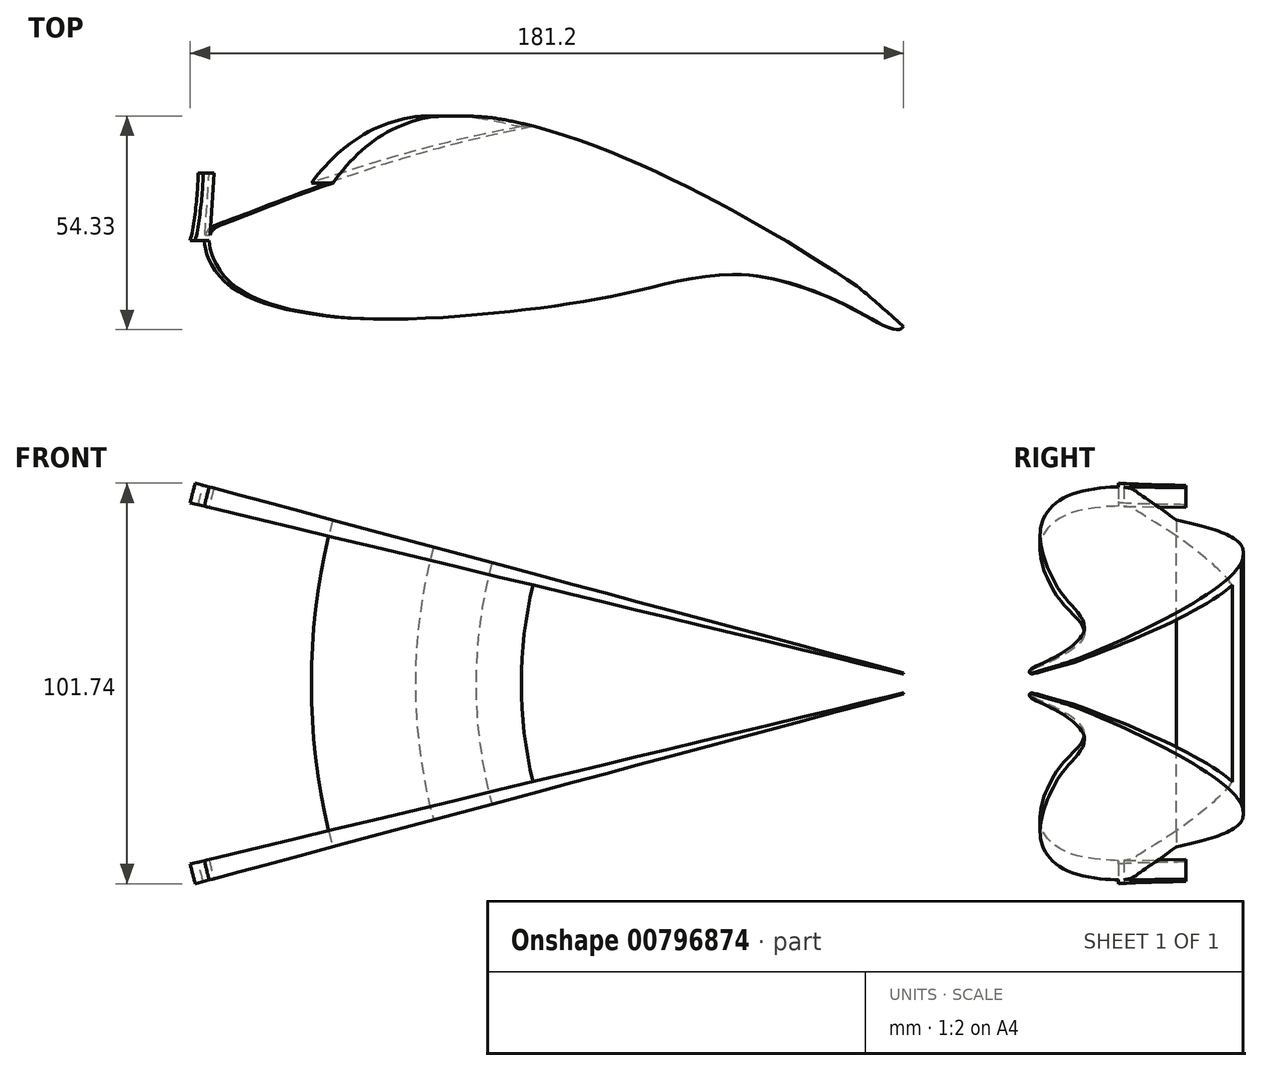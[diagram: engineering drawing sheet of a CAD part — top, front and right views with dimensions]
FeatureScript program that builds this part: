
annotation { "Feature Type Name" : "Feature", "Feature Type Description" : "" }
export const myFeature = defineFeature(function(context is Context, id is Id, definition is map)
    precondition{}
    {
        {
            var Q0;
            Q0=qCreatedBy(makeId("Top.planeOp"),FACE);
            var sketch = newSketch(context, id + "F0", { "sketchPlane" : qUnion([Q0])});
            skFitSpline(sketch, "E0", {"points": [v(-170.18, 31.8) * mm, v(-106.5, 38.35) * mm, v(-30.65, 17.74) * mm, v(27.4, -25.33) * mm, v(47.07, -59.04) * mm, v(24.6, -41.25) * mm, v(-86.84, 1.83) * mm, v(-156.13, -10.35) * mm, v(-170.18, 31.8) * mm]});
            skLineSegment(sketch, "E1", {"start": v(-156.13, -10.35) * mm, "end": v(-156.13, -10.35) * mm});
            skLineSegment(sketch, "E2", {"start": v(-156.13, 31.8) * mm, "end": v(-156.13, 31.8) * mm});
            skFitSpline(sketch, "E3", {"points": [v(-156.13, -10.35) * mm, v(-143.58, -45.36) * mm, v(-112.26, -54.53) * mm, v(-67.18, -53) * mm, v(-33.57, -46.89) * mm, v(-4.54, -43.83) * mm, v(24.49, -51.47) * mm, v(40.73, -54.96) * mm, v(24.6, -41.25) * mm, v(-86.84, 1.83) * mm, v(-128.3, -41.25) * mm], "startDerivative": vector(76.26, -423.63) * mm, "endDerivative": vector(-240.52, -486.65) * mm});
            skLineSegment(sketch, "E4", {"start": v(47.07, -59.04) * mm, "end": v(47.07, -80.17) * mm});
            skLineSegment(sketch, "E5", {"start": v(47.07, -59.04) * mm, "end": v(47.07, -18.21) * mm});
            skFitSpline(sketch, "E6", {"points": [v(-156.13, 40.59) * mm, v(-151.83, 31.31) * mm, v(-148.5, 17.34) * mm, v(-147.45, -1.95) * mm, v(-148.02, -21.15) * mm, v(-151.28, -31.75) * mm, v(-156.13, 40.59) * mm]});
            skFitSpline(sketch, "E7", {"points": [v(-145.6, -31.34) * mm, v(-140.42, -40.15) * mm, v(-112.45, -48.95) * mm, v(-66.86, -47.66) * mm, v(-34.74, -42.74) * mm, v(-5.2, -38.33) * mm, v(25.36, -47.92) * mm, v(36.8, -51.47) * mm, v(0, -2.85) * mm, v(-138.35, -24.09) * mm, v(-144.57, -26.68) * mm, v(-145.6, -28.23) * mm, v(-145.6, -31.34) * mm]});
            skLineSegment(sketch, "E8", {"start": v(-145.6, -28.23) * mm, "end": v(-144.57, -12.5) * mm});
            skLineSegment(sketch, "E9", {"start": v(-149.5, -29.67) * mm, "end": v(-145.6, -29.67) * mm});
            skSolve(sketch);
        }
        {
            var Q0;
            {var subQ5=sQuery(id+"F0.wireOp",EDGE,"E3");Q0=makeQuery(id+"F0.imprint","IMPRINT",FACE,{"disambiguationData":[TD([[makeQuery(id+"F0.imprint","IMPRINT",EDGE,{"derivedFrom":subQ5}),1.0]])]});}
            var Q1;
            {var subQ5=sQuery(id+"F0.wireOp",EDGE,"E7");Q1=makeQuery(id+"F0.imprint","IMPRINT",FACE,{"disambiguationData":[TD([[makeQuery(id+"F0.imprint","IMPRINT",EDGE,{"derivedFrom":subQ5}),1.0]])]});}
            var Q2;
            {var subQ0=sQuery(id+"F0.wireOp",EDGE,"E8");Q2=makeQuery(id+"F0.imprint","IMPRINT",FACE,{"disambiguationData":[TD([[makeQuery(id+"F0.imprint","IMPRINT",EDGE,{"derivedFrom":subQ0}),1.0]])]});}
            var Q3;
            Q3=sQuery(id+"F0.wireOp",EDGE,"E5");
            revolve(context, id + "F1", {"surfaceOperationType" : NewSurfaceOperationType.NEW, "entities" : qUnion([Q0, Q1, Q2]), "axis" : qUnion([Q3]), "revolveType" : RevolveType.SYMMETRIC, "angle" : 30 * degree});
        }
        {
            var Q0;
            {var subQ5=sQuery(id+"F0.wireOp",EDGE,"E7");Q0=makeQuery(id+"F0.imprint","IMPRINT",FACE,{"disambiguationData":[TD([[makeQuery(id+"F0.imprint","IMPRINT",EDGE,{"derivedFrom":subQ5}),1.0]])]});}
            var Q1;
            {var subQ0=sQuery(id+"F0.wireOp",EDGE,"E8");Q1=makeQuery(id+"F0.imprint","IMPRINT",FACE,{"disambiguationData":[TD([[makeQuery(id+"F0.imprint","IMPRINT",EDGE,{"derivedFrom":subQ0}),1.0]])]});}
            var Q2;
            Q2=sQuery(id+"F0.wireOp",EDGE,"E5");
            revolve(context, id + "F2", {"operationType" : NewBodyOperationType.REMOVE, "surfaceOperationType" : NewSurfaceOperationType.NEW, "entities" : qUnion([Q0, Q1]), "axis" : qUnion([Q2]), "revolveType" : RevolveType.SYMMETRIC, "oppositeDirection" : true, "angle" : 27 * degree});
        }
    });
